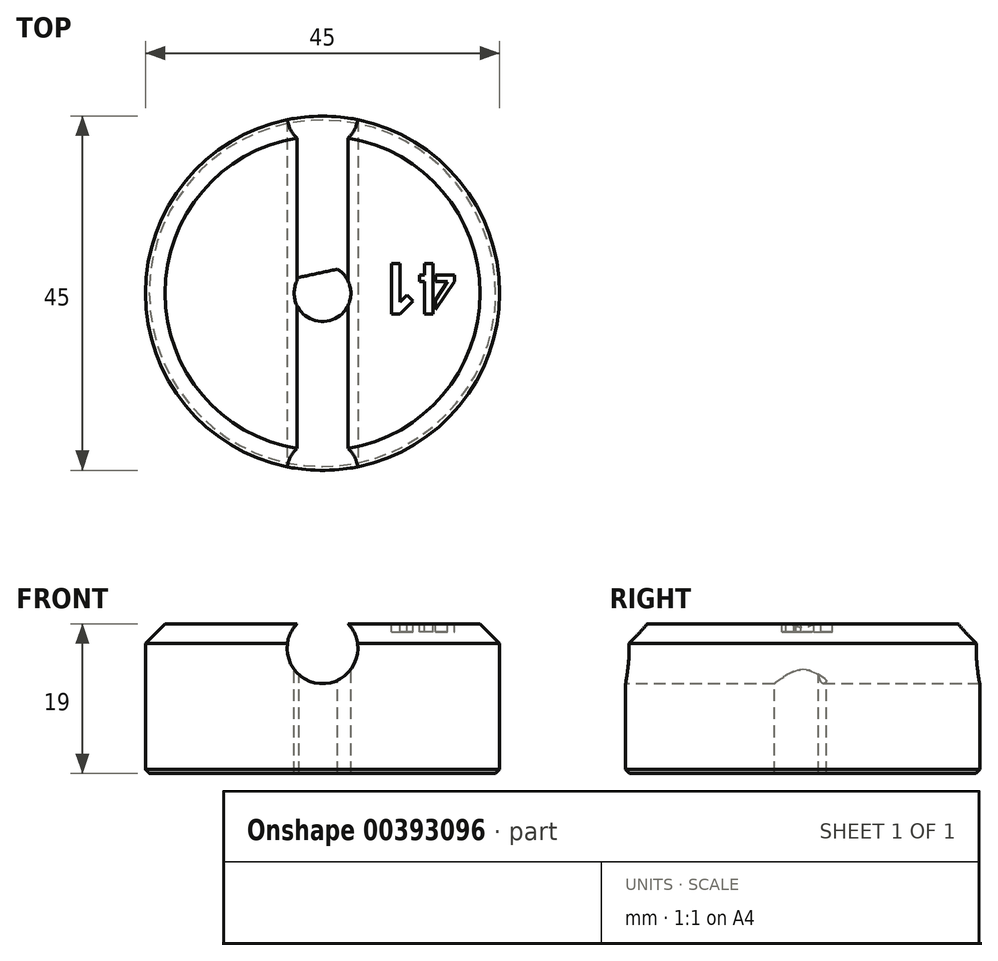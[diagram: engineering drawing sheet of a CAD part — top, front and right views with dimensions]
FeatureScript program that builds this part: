
annotation { "Feature Type Name" : "Feature", "Feature Type Description" : "" }
export const myFeature = defineFeature(function(context is Context, id is Id, definition is map)
    precondition{}
    {
        {
            var Q0;
            Q0=qCreatedBy(makeId("Top.planeOp"),FACE);
            var sketch = newSketch(context, id + "F0", { "sketchPlane" : qUnion([Q0])});
            skCircle(sketch, "E0", {"center": v(0, 0) * mm, "radius": 3.6 * mm});
            skCircle(sketch, "E1", {"center": v(0, 0) * mm, "radius": 22.5 * mm});
            skLineSegment(sketch, "E2", {"start": v(-1.91, 3.05) * mm, "end": v(2.98, 2.02) * mm});
            skSolve(sketch);
        }
        {
            var Q0;
            Q0=makeQuery(id+"F0.imprint","IMPRINT",FACE,{"disambiguationData":[TD([[makeQuery(id+"F0.imprint","IMPRINT",EDGE,{"derivedFrom":sQuery(id+"F0.wireOp",EDGE,"E0")}),-1.0]])]});
            var Q1;
            {var subQ0=sQuery(id+"F0.wireOp",EDGE,"E2");Q1=makeQuery(id+"F0.imprint","IMPRINT",FACE,{"disambiguationData":[TD([[makeQuery(id+"F0.imprint","IMPRINT",EDGE,{"derivedFrom":subQ0}),1.0]])]});}
            extrude(context, id + "F1", {"entities" : qUnion([Q0, Q1]), "depth" : 18 * mm, "hasSecondDirection" : true, "secondDirectionOppositeDirection" : true, "secondDirectionDepth" : 1 * mm});
        }
        {
            var Q0;
            Q0=qCreatedBy(makeId("Front.planeOp"),FACE);
            var sketch = newSketch(context, id + "F2", { "sketchPlane" : qUnion([Q0])});
            skCircle(sketch, "E3", {"center": v(0, 2.1) * mm, "radius": 4.5 * mm});
            skSolve(sketch);
        }
        {
            var Q0;
            Q0 = qSketchRegion(id + "F2", true);
            extrude(context, id + "F3", {"entities" : qUnion([Q0]), "operationType" : NewBodyOperationType.REMOVE, "oppositeDirection" : true, "depth" : 60 * mm, "symmetric" : true});
        }
        {
            var Q0;
            Q0=makeQuery(id+"F3.boolean.opBoolean","SPLIT",EDGE,{"disambiguationData":[OD(1.0)],"derivedFrom":makeQuery(id+"F1.opExtrude","CAP_EDGE",EDGE,{"disambiguationData":[OSD([sQuery(id+"F0.wireOp",EDGE,"E1")])],"isStart":true})});
            var Q1;
            Q1=makeQuery(id+"F3.boolean.opBoolean","SPLIT",EDGE,{"disambiguationData":[OD(0.0)],"derivedFrom":makeQuery(id+"F1.opExtrude","CAP_EDGE",EDGE,{"disambiguationData":[OSD([sQuery(id+"F0.wireOp",EDGE,"E1")])],"isStart":true})});
            chamfer(context, id + "F4", {"entities" : qUnion([Q0, Q1]), "width" : 2.5 * mm, "tangentPropagation" : true});
        }
        {
            var Q0;
            Q0=makeQuery(id+"F3.boolean.opBoolean","SPLIT",FACE,{"disambiguationData":[OD(1.0)],"derivedFrom":makeQuery(id+"F1.opExtrude","CAP_FACE",FACE,{"disambiguationData":[OSD([sQuery(id+"F0.wireOp",EDGE,"E0"),sQuery(id+"F0.wireOp",EDGE,"E1")])],"isStart":true})});
            var sketch = newSketch(context, id + "F5", { "sketchPlane" : qUnion([Q0])});
            skText(sketch, "E4", { "text": "41", "fontName": "AllertaStencil-Regular.ttf"});
            const initialGuessF5  = {"E4": [-0.01712, -0.00378, 1, 0, 0.0064]};
            skSetInitialGuess(sketch, initialGuessF5);
            skSolve(sketch);
        }
        {
            var Q0;
            Q0 = qSketchRegion(id + "F5", true);
            extrude(context, id + "F6", {"entities" : qUnion([Q0]), "operationType" : NewBodyOperationType.REMOVE, "oppositeDirection" : true, "depth" : 1 * mm});
        }
        {
            var Q0;
            Q0=makeQuery(id+"F1.opExtrude","SWEPT_BODY",BODY,{"disambiguationData":[OSD([sQuery(id+"F0.wireOp",EDGE,"E0"),sQuery(id+"F0.wireOp",EDGE,"E1"),sQuery(id+"F0.wireOp",EDGE,"E2")])]});
            var Q1;
            Q1=sQuery(id+"F0.wireOp",VERTEX,"E1.center");
            var Q2;
            Q2=makeQuery(id+"F3.boolean.opBoolean","INTERSECT",EDGE,{"disambiguationData":[OD(1.0)],"derivedFrom":[makeQuery(id+"F1.opExtrude","CAP_FACE",FACE,{"disambiguationData":[OSD([sQuery(id+"F0.wireOp",EDGE,"E0"),sQuery(id+"F0.wireOp",EDGE,"E1"),sQuery(id+"F0.wireOp",EDGE,"E2")])],"isStart":true}),makeQuery(id+"F3.opExtrude","SWEPT_FACE",FACE,{"disambiguationData":[OSD([sQuery(id+"F2.wireOp",EDGE,"E3")])]})]});
            transform(context, id + "F7", {"entities" : qUnion([Q0]), "transformType" : TransformType.ROTATION, "transformAxis" : qUnion([Q2]), "angle" : 180 * degree, "makeCopy" : false});
        }
        {
            var Q0;
            Q0=makeQuery(id+"F1.opExtrude","CAP_EDGE",EDGE,{"disambiguationData":[OSD([sQuery(id+"F0.wireOp",EDGE,"E1")])],"isStart":false});
            chamfer(context, id + "F8", {"entities" : qUnion([Q0]), "width" : .5 * mm, "tangentPropagation" : true});
        }
    });
